# Revit family: PGLTD_BSLTD_DetailComponent_ColdRoofConstruction_Roofshield_EavesDetail
name_source: partatom
category: Detail Items
revit_build: Autodesk Revit 2015 (Build: 20140606_1530(x64)
units: mm (PartAtom-declared; Revit-internal decimal feet)

## types (2) — shared parameters
BattenDepth = 25 mm  [stored 0.082021 ft]
CementitiousBoardThickness = 13 mm
FacadeThickness = 100 mm  [stored 0.328084 ft]
Gutter = 130.00°
PlasterboardCeilingThickness = 13 mm
PlasterboardLiningThickness = 13 mm
RoofPitch = 40.00°
StructuralFrameThickness = 150 mm  [stored 0.492126 ft]
TimberJoistDepth = 195 mm  [stored 0.639764 ft]
WallCavityThickness = 50 mm  [stored 0.164042 ft]

## per-type parameters (varying)
| type | Sarking | SarkingThickness |
| WithSarking | Yes | 13 mm |
| NoSarking | No | 0 mm  [stored 0 ft] |

note: [stored X ft] marks values corroborated as IEEE doubles in the binary element streams (Revit-internal decimal feet)

## geometry (parser evidence)
native form markers: Blend x2, Sweep x5
no freeform markers — native parametric forms only
